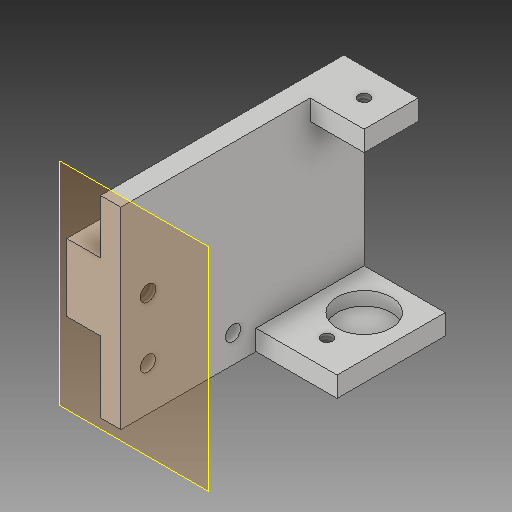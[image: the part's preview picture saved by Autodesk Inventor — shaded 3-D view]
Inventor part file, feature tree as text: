
AUTODESK INVENTOR PART (.ipt)
format: ipt  version: 2017 SP1 (Build 210196100, 196)  size: 202,240 bytes
history: native  units: in
note: dims shown in document units (in); Inventor stores cm internally (conversion verified against a paired STEP export)
features: projected_geometry x9, sketch x8, hole x5, extrude x4, plane x1, mirror x1
ambient origin geometry x8: Origin, YZ Plane, XZ Plane, XY Plane, X Axis, Y Axis, Z Axis, Center Point
bodies: Solid1 (feature_tree)
feature tree (28):
  extrude  "Extrusion1"  Depth=2.25in
  extrude  "Extrusion2"  Depth=0.5in
  extrude  "Extrusion3"  Depth=0.5in TaperAngle=0.0deg
  extrude  "Extrusion4"  Depth=0.75in TaperAngle=0.0deg
  hole  "Hole1"  [1 undecoded]
  hole  "Hole2"  [1 undecoded]
  hole  "Hole3"  [1 undecoded]
  hole  "Hole4"  [1 undecoded]
  plane  "Work Plane1"
  mirror  "Mirror1"
  hole  "Hole5"  [1 undecoded]
  sketch  "Sketch1"  dims[d0=1.7812in d1=2.25in]
  sketch  "Sketch2"  dims[d2=0.1875in d3=0.0in d4=0.5in]
  projected_geometry  "Projected Loop1"
  sketch  "Sketch3"  dims[d5=0.1875in d6=0.5in d7=0.0in]
  projected_geometry  "Projected Loop2"
  projected_geometry  "Projected Loop3"
  sketch  "Sketch5"  dims[d8=0.1875in d9=0.75in d10=0.0in]
  projected_geometry  "Projected Loop4"
  projected_geometry  "Projected Loop5"
  sketch  "Sketch6"  dims[d13=0.3125in d14=0.0in d15=0.1875in]
  projected_geometry  "Projected Loop6"
  sketch  "Sketch10"  dims[d16=0.8125in d17=0.25in]
  projected_geometry  "Projected Loop10"
  sketch  "Sketch11"  dims[d18=0.145in d19=0.38in d20=0.375in d21=0.25in d22=0.5635in d23=0.588in d24=0.8108in d25=0.375in]
  projected_geometry  "Projected Loop11"
  sketch  "Sketch12"  dims[d26=0.375in d27=0.5in d28=0.75in d29=0.375in d30=0.25in d31=0.5635in d32=0.125in d33=0.0in d48=0.625in d49=0.5in d50=0.5in d51=0.104in d52=0.276in d53=0.375in d54=0.25in d55=0.5635in d56=0.432in d57=0.8108in d58=0.25in d59=0.104in d60=0.276in d61=0.375in d62=0.25in d63=0.5635in d64=0.432in d65=0.8108in d66=0.406in d67=0.25in d68=0.256in d69=1.0375in d70=0.14in d71=0.75in d72=0.375in d73=0.25in d74=0.5635in d75=1.0in d76=0.8108in]
  projected_geometry  "Projected Loop12"
note: 5 required parameter values undecoded (feature->parameter linkage not recoverable at this tier; creation-order binding heuristic only, values carry confidence <= 0.55)
